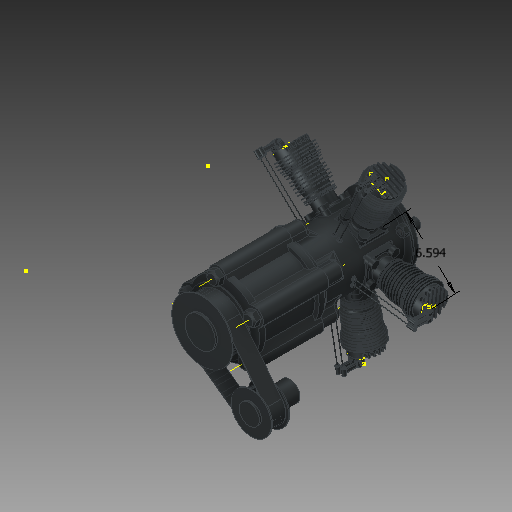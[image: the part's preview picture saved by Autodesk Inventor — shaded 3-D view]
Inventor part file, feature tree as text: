
AUTODESK INVENTOR PART (.ipt)
format: ipt  version: 2018 (Build 220112000, 112)  size: 6,024,192 bytes
history: native  units: in
note: dims shown in document units (in); Inventor stores cm internally (conversion verified against a paired STEP export)
features: other x109, sketch x16, extrude x1
ambient origin geometry x8: Origin, YZ Plane, XZ Plane, XY Plane, X Axis, Y Axis, Z Axis, Center Point
bodies: Solid1 (feature_tree), Solid2 (feature_tree), Solid3 (feature_tree), Solid4 (feature_tree), Solid5 (feature_tree), Solid6 (feature_tree), Solid7 (feature_tree), Solid8 (feature_tree), Solid9 (feature_tree), Solid10 (feature_tree), Solid11 (feature_tree), Solid12 (feature_tree), Solid13 (feature_tree), Solid14 (feature_tree), Solid15 (feature_tree), Solid16 (feature_tree), Solid17 (feature_tree), Solid18 (feature_tree), Solid19 (feature_tree), Solid20 (feature_tree), Solid21 (feature_tree), Solid22 (feature_tree), Solid23 (feature_tree), Solid24 (feature_tree), Solid25 (feature_tree), Solid26 (feature_tree), Solid27 (feature_tree), Solid28 (feature_tree), Solid29 (feature_tree), Solid30 (feature_tree), Solid31 (feature_tree), Solid32 (feature_tree), Solid33 (feature_tree), Solid34 (feature_tree), Solid35 (feature_tree), Solid36 (feature_tree), Solid37 (feature_tree), Solid38 (feature_tree), Solid39 (feature_tree), Solid40 (feature_tree), Solid41 (feature_tree), Solid42 (feature_tree), Solid43 (feature_tree), Solid44 (feature_tree), Solid45 (feature_tree), Solid46 (feature_tree), Solid47 (feature_tree), Solid48 (feature_tree), Solid49 (feature_tree), Solid50 (feature_tree), Solid51 (feature_tree), Solid52 (feature_tree), Solid53 (feature_tree), Solid54 (feature_tree), Solid55 (feature_tree), Solid56 (feature_tree), Solid57 (feature_tree), Solid58 (feature_tree), Solid59 (feature_tree), Solid60 (feature_tree), Solid61 (feature_tree), Solid62 (feature_tree), Solid63 (feature_tree), Solid64 (feature_tree), Solid65 (feature_tree), Solid66 (feature_tree), Solid67 (feature_tree), Solid68 (feature_tree), Solid69 (feature_tree), Solid70 (feature_tree), Solid71 (feature_tree), Solid72 (feature_tree), Solid73 (feature_tree), Solid74 (feature_tree), Solid75 (feature_tree), Solid76 (feature_tree), Solid77 (feature_tree), Solid78 (feature_tree), Solid79 (feature_tree), Solid80 (feature_tree), Solid81 (feature_tree), Solid82 (feature_tree), Solid83 (feature_tree), Solid84 (feature_tree), Solid85 (feature_tree), Solid86 (feature_tree), Solid87 (feature_tree), Solid88 (feature_tree), Solid89 (feature_tree)
feature tree (126):
  other  "17032021.iam"
  other  "cylinder asm.iam:1::inner.ipt:1"
  other  "cylinder asm.iam:1::outer.ipt:1"
  other  "cylinder asm.iam:1::lip plate.ipt:1"
  other  "cylinder asm.iam:1::bolt M12x45.ipt:1"
  other  "cylinder asm.iam:1::nut M12.ipt:1"
  other  "cylinder asm.iam:1::nut M12.ipt:2"
  other  "cylinder asm.iam:1::bolt M12x45.ipt:2"
  other  "cylinder asm.iam:1::nut M12.ipt:3"
  other  "cylinder asm.iam:1::bolt M12x45.ipt:3"
  other  "cylinder asm.iam:1::nut M12.ipt:4"
  other  "cylinder asm.iam:1::bolt M12x45.ipt:4"
  other  "cylinder asm.iam:1::nut M12.ipt:5"
  other  "cylinder asm.iam:1::bolt M12x45.ipt:5"
  other  "cylinder asm.iam:1::bolt M20x200.ipt:1"
  other  "cylinder asm.iam:1::bolt M20x200.ipt:2"
  other  "cylinder asm.iam:1::bolt M20x200.ipt:3"
  other  "cylinder asm.iam:1::bolt M20x200.ipt:4"
  other  "cylinder asm.iam:1::bolt M20x200.ipt:5"
  other  "cylinder asm.iam:1::vertical cylinder.ipt:1"
  other  "cylinder asm.iam:1::vertical cylinder.ipt:2"
  other  "cylinder asm.iam:1::vertical cylinder.ipt:3"
  other  "cylinder asm.iam:1::vertical cylinder.ipt:4"
  other  "cylinder asm.iam:1::vertical cylinder.ipt:5"
  other  "cylinder asm.iam:1::bolt M10x36.ipt:1"
  other  "cylinder asm.iam:1::bolt M10x36.ipt:2"
  other  "cylinder asm.iam:1::bolt M10x36.ipt:3"
  other  "cylinder asm.iam:1::bolt M10x36.ipt:4"
  other  "cylinder asm.iam:1::bolt M10x36.ipt:5"
  other  "cylinder asm.iam:1::bolt M10x36.ipt:6"
  other  "cylinder asm.iam:1::bolt M10x36.ipt:7"
  other  "cylinder asm.iam:1::bolt M10x36.ipt:8"
  other  "cylinder asm.iam:1::bolt M10x36.ipt:9"
  other  "cylinder asm.iam:1::bolt M10x36.ipt:10"
  other  "cylinder asm.iam:1::bolt M10x36.ipt:11"
  other  "cylinder asm.iam:1::bolt M10x36.ipt:12"
  other  "cylinder asm.iam:1::bolt M10x36.ipt:13"
  other  "cylinder asm.iam:1::bolt M10x36.ipt:14"
  other  "cylinder asm.iam:1::bolt M10x36.ipt:15"
  other  "cylinder asm.iam:1::bolt M10x36.ipt:16"
  other  "cylinder asm.iam:1::bolt M10x36.ipt:17"
  other  "cylinder asm.iam:1::bolt M10x36.ipt:18"
  other  "cylinder asm.iam:1::bolt M10x36.ipt:19"
  other  "cylinder asm.iam:1::bolt M10x36.ipt:20"
  other  "cylinder asm.iam:1::pin.ipt:1"
  other  "cylinder asm.iam:1::knuckle.ipt:1"
  other  "cylinder asm.iam:1::knuckle.ipt:2"
  other  "cylinder asm.iam:1::lower pin.ipt:1"
  other  "cylinder asm.iam:1::lower pin.ipt:2"
  other  "cylinder asm.iam:1::lower pin.ipt:3"
  other  "cylinder asm.iam:1::supporting rod.ipt:1"
  other  "cylinder asm.iam:1::supporting rod.ipt:2"
  other  "cylinder asm.iam:1::lower pin.ipt:4"
  other  "cylinder asm.iam:1::lower pin.ipt:5"
  other  "cylinder asm.iam:1::supporting rod.ipt:3"
  other  "cylinder asm.iam:1::supporting rod.ipt:4"
  other  "cylinder asm.iam:1::lower pin.ipt:6"
  other  "cylinder asm.iam:1::lower pin.ipt:7"
  other  "cylinder asm.iam:1::lower pin.ipt:8"
  other  "cylinder asm.iam:1::knuckle.ipt:3"
  other  "cylinder asm.iam:1::knuckle.ipt:4"
  other  "cylinder asm.iam:1::pin.ipt:2"
  other  "cylinder asm.iam:1::lower pin.ipt:9"
  other  "cylinder asm.iam:1::supporting rod.ipt:5"
  other  "cylinder asm.iam:1::supporting rod.ipt:6"
  other  "cylinder asm.iam:1::lower pin.ipt:10"
  other  "cylinder asm.iam:1::lower pin.ipt:11"
  other  "cylinder asm.iam:1::lower pin.ipt:12"
  other  "cylinder asm.iam:1::knuckle.ipt:5"
  other  "cylinder asm.iam:1::knuckle.ipt:6"
  other  "cylinder asm.iam:1::pin.ipt:3"
  other  "cylinder asm.iam:1::lower pin.ipt:13"
  other  "cylinder asm.iam:1::supporting rod.ipt:7"
  other  "cylinder asm.iam:1::supporting rod.ipt:8"
  other  "cylinder asm.iam:1::lower pin.ipt:14"
  other  "cylinder asm.iam:1::lower pin.ipt:15"
  other  "cylinder asm.iam:1::lower pin.ipt:16"
  other  "cylinder asm.iam:1::knuckle.ipt:7"
  other  "cylinder asm.iam:1::knuckle.ipt:8"
  other  "cylinder asm.iam:1::pin.ipt:4"
  other  "cylinder asm.iam:1::lower pin.ipt:17"
  other  "cylinder asm.iam:1::supporting rod.ipt:9"
  other  "cylinder asm.iam:1::supporting rod.ipt:10"
  other  "cylinder asm.iam:1::lower pin.ipt:18"
  other  "cylinder asm.iam:1::lower pin.ipt:19"
  other  "cylinder asm.iam:1::lower pin.ipt:20"
  other  "cylinder asm.iam:1::knuckle.ipt:9"
  other  "cylinder asm.iam:1::knuckle.ipt:10"
  other  "cylinder asm.iam:1::pin.ipt:5"
  other  "chain sproket.ipt:1"
  sketch  "Sketch14"
  extrude  "Extrusion1"  Depth=0.3937in
  sketch  "Sketch16"
  sketch  "Sketch17"
  other  "Work Axis1"
  other  "Work Axis1_1"
  other  "Work Axis1_2"
  other  "Work Axis1_3"
  other  "Work Axis1_4"
  other  "Work Axis1_5"
  other  "Work Axis1_6"
  other  "Work Axis1_7"
  other  "Work Axis1_8"
  other  "Work Axis1_9"
  other  "Work Axis1_10"
  other  "Work Axis1_11"
  other  "Work Axis1_12"
  other  "Work Axis1_13"
  sketch  "Sketch9"
  other  "Work Axis1_14"
  sketch  "Sketch9_1"  dims[d0=0.3937in d1=1.969in]
  other  "Work Axis1_15"
  sketch  "Sketch9_2"
  other  "Work Axis1_16"
  sketch  "Sketch9_3"
  other  "Work Axis1_17"
  sketch  "Sketch9_4"
  other  "Work Axis1_18"
  sketch  "Sketch1"  dims[d2=2.0in d3=0.0in]
  sketch  "Sketch1_1"  dims[d4=6.594in]
  sketch  "Sketch1_2"
  sketch  "Sketch1_3"
  sketch  "Sketch1_4"
  sketch  "Sketch2"
  sketch  "Sketch11"
  sketch  "Sketch15"
